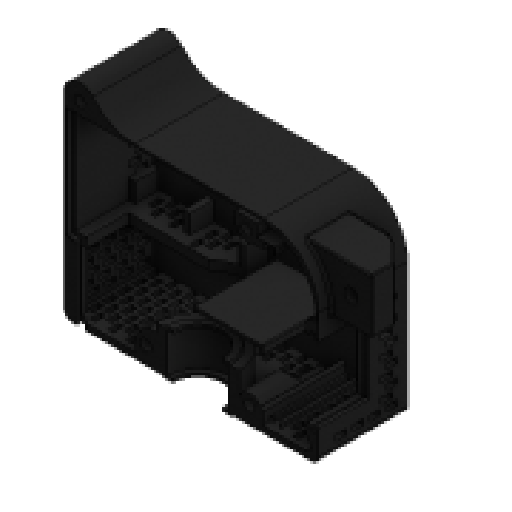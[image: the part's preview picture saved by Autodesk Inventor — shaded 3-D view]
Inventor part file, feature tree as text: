
AUTODESK INVENTOR PART (.ipt)
format: ipt  version: 2023 (Build 270158000, 158)  size: 1,475,072 bytes
history: native  units: mm
features: extrude x1, sketch x1, other x1, projected_geometry x1
ambient origin geometry x8: Origin, YZ Plane, XZ Plane, XY Plane, X Axis, Y Axis, Z Axis, Center Point
bodies: Solid1 (feature_tree), Solid2 (feature_tree)
feature tree (4):
  extrude  "Extrusion1"  [1 undecoded]
  sketch  "Sketch1"  dims[d0=10.0mm d1=0.0mm]
  other  "_Body_Drawing_-_Fillet22_"
  projected_geometry  "Project Cut Edges1"
note: 1 required parameter value undecoded (feature->parameter linkage not recoverable at this tier; creation-order binding heuristic only, values carry confidence <= 0.55)
